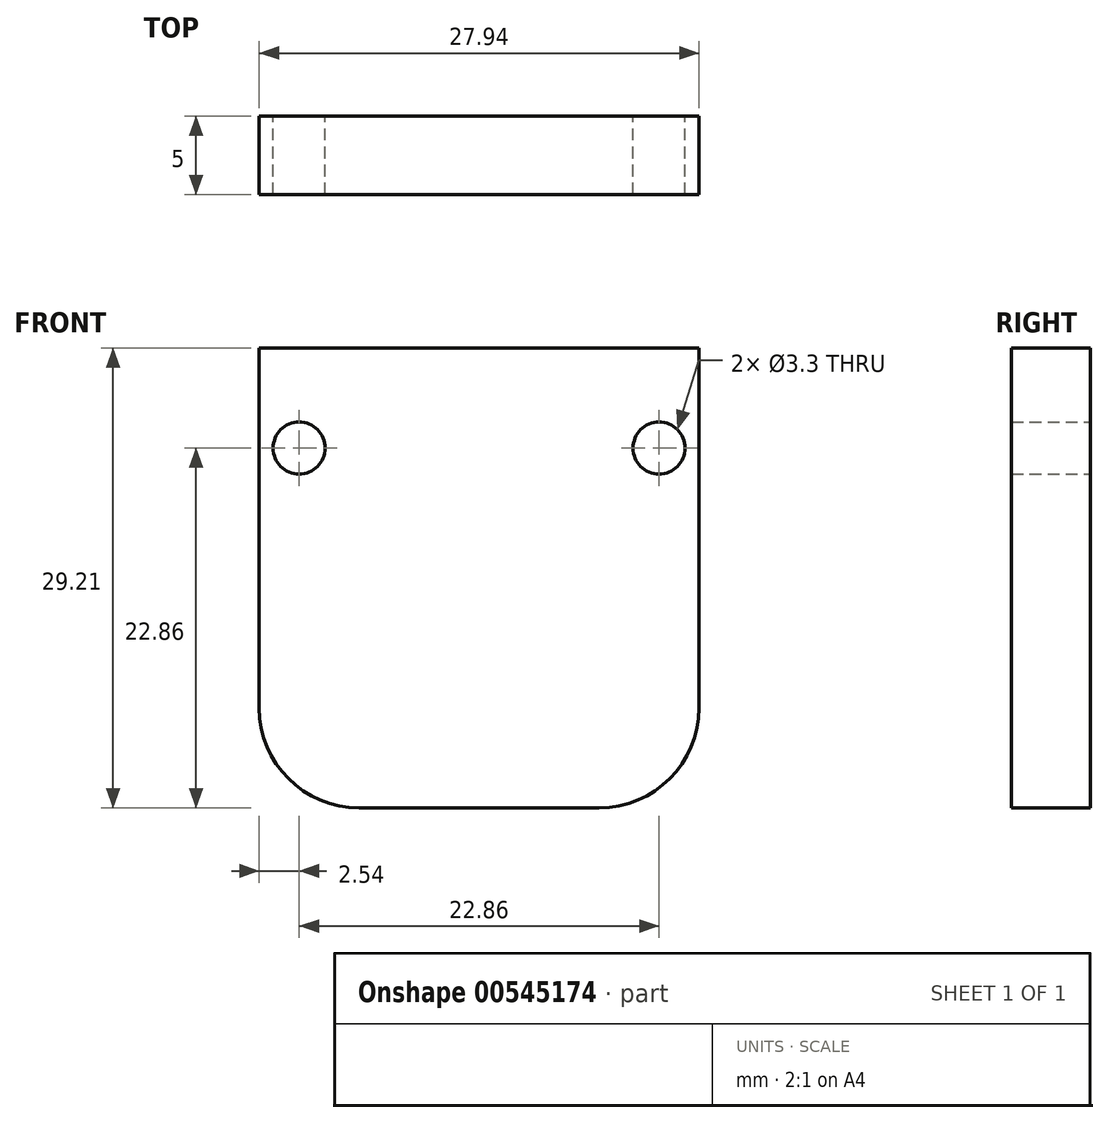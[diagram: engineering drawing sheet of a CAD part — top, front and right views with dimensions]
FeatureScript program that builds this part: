
annotation { "Feature Type Name" : "Feature", "Feature Type Description" : "" }
export const myFeature = defineFeature(function(context is Context, id is Id, definition is map)
    precondition{}
    {
        {
            var Q0;
            Q0=qCreatedBy(makeId("Front.planeOp"),FACE);
            var sketch = newSketch(context, id + "F0", { "sketchPlane" : qUnion([Q0])});
            skLineSegment(sketch, "E0.bottom", {"start": v(-27.94, 0) * mm, "end": v(0, 0) * mm});
            skLineSegment(sketch, "E0.top", {"start": v(-21.6, -29.21) * mm, "end": v(-6.35, -29.21) * mm});
            skLineSegment(sketch, "E0.left", {"start": v(-27.94, 0) * mm, "end": v(-27.94, -22.86) * mm});
            skLineSegment(sketch, "E0.right", {"start": v(0, 0) * mm, "end": v(0, -22.86) * mm});
            skCircle(sketch, "E1", {"center": v(-25.4, -6.35) * mm, "radius": 1.65 * mm});
            skCircle(sketch, "E2", {"center": v(-2.54, -6.35) * mm, "radius": 1.65 * mm});
            skPoint(sketch, "E3.visualSharp", {"position": v(-27.94, -29.21) * mm});
            skArc(sketch, "E3.filletArc", {"start": v(-27.94, -22.86) * mm, "mid": v(-26.08, -27.35) * mm, "end": v(-21.6, -29.21) * mm});
            skPoint(sketch, "E4.visualSharp", {"position": v(0, -29.21) * mm});
            skArc(sketch, "E4.filletArc", {"start": v(-6.35, -29.21) * mm, "mid": v(-1.86, -27.35) * mm, "end": v(0, -22.86) * mm});
            skSolve(sketch);
        }
        {
            var Q0;
            Q0=makeQuery(id+"F0.imprint","IMPRINT",FACE,{"disambiguationData":[TD([[makeQuery(id+"F0.imprint","IMPRINT",EDGE,{"derivedFrom":sQuery(id+"F0.wireOp",EDGE,"E0.bottom")}),-1.0]])]});
            extrude(context, id + "F1", {"entities" : qUnion([Q0]), "depth" : 5 * mm, "offsetDistance" : 25.4 * mm});
        }
    });
